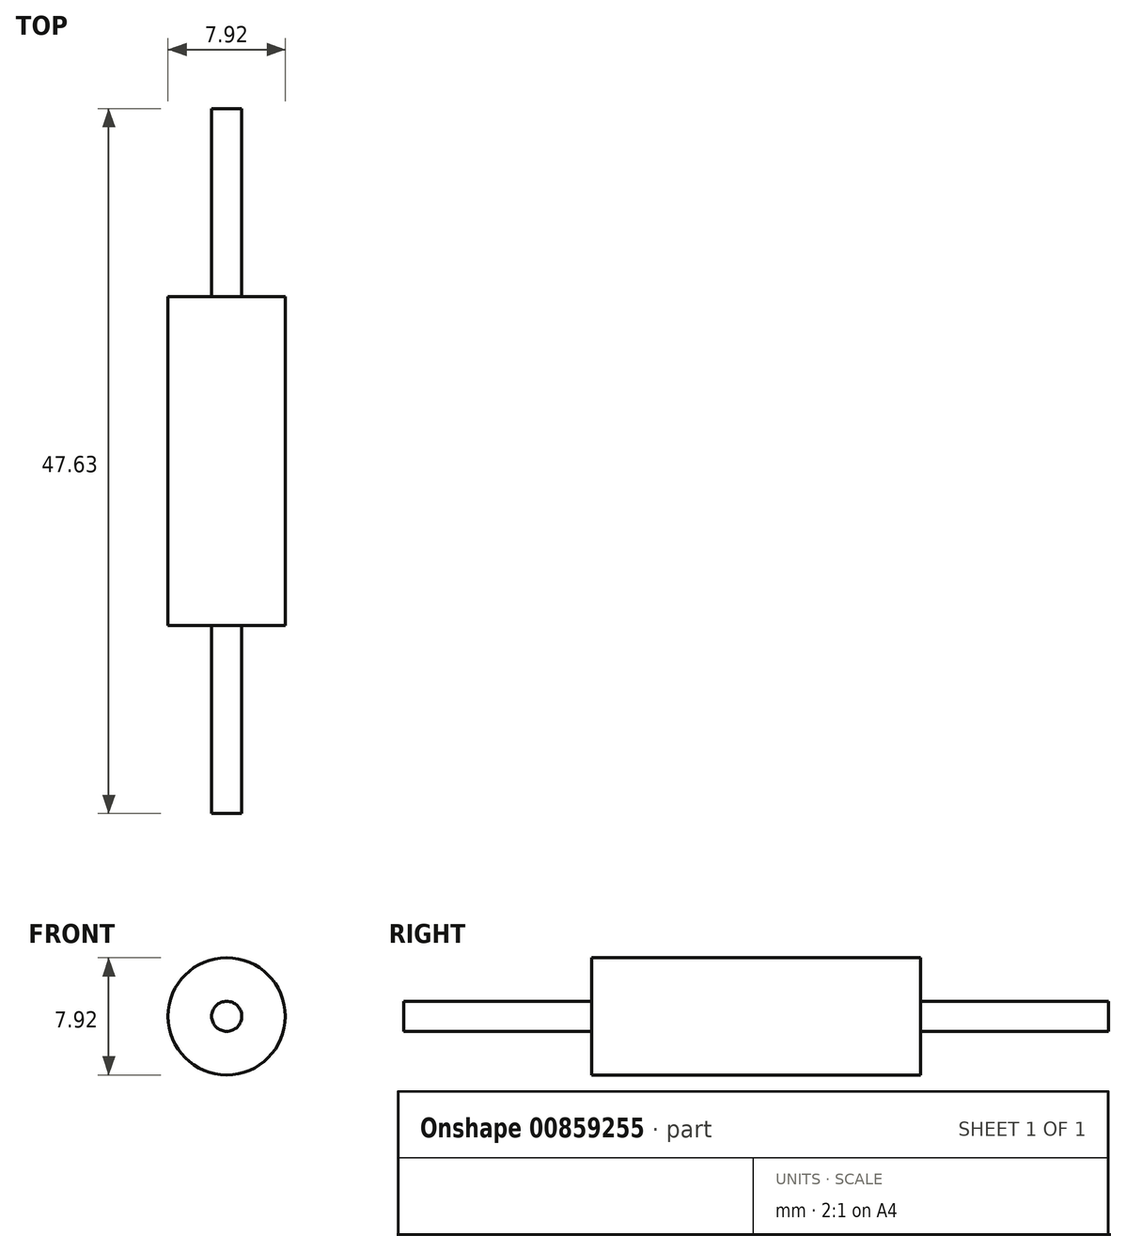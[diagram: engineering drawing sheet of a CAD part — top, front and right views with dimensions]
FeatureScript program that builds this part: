
annotation { "Feature Type Name" : "Feature", "Feature Type Description" : "" }
export const myFeature = defineFeature(function(context is Context, id is Id, definition is map)
    precondition{}
    {
        {
            var Q0;
            Q0=qCreatedBy(makeId("Front.planeOp"),FACE);
            var sketch = newSketch(context, id + "F0", { "sketchPlane" : qUnion([Q0])});
            skCircle(sketch, "E0", {"center": v(0, 0) * mm, "radius": 3.96 * mm});
            skSolve(sketch);
        }
        {
            var Q0;
            Q0 = qSketchRegion(id + "F0", true);
            extrude(context, id + "F1", {"entities" : qUnion([Q0]), "oppositeDirection" : true, "depth" : 22.22 * mm, "offsetDistance" : 25.4 * mm});
        }
        {
            var Q0;
            Q0=makeQuery(id+"F1.opExtrude","CAP_FACE",FACE,{"disambiguationData":[OSD([sQuery(id+"F0.wireOp",EDGE,"E0")])],"isStart":true});
            var sketch = newSketch(context, id + "F2", { "sketchPlane" : qUnion([Q0])});
            skCircle(sketch, "E1", {"center": v(0, 0) * mm, "radius": 1.02 * mm});
            skSolve(sketch);
        }
        {
            var Q0;
            Q0 = qSketchRegion(id + "F2", true);
            extrude(context, id + "F3", {"entities" : qUnion([Q0]), "operationType" : NewBodyOperationType.ADD, "depth" : 12.7 * mm, "offsetDistance" : 25.4 * mm});
        }
        {
            var Q0;
            Q0=makeQuery(id+"F1.opExtrude","CAP_FACE",FACE,{"disambiguationData":[OSD([sQuery(id+"F0.wireOp",EDGE,"E0")])],"isStart":false});
            var sketch = newSketch(context, id + "F4", { "sketchPlane" : qUnion([Q0])});
            skCircle(sketch, "E2", {"center": v(0, 0) * mm, "radius": 1.02 * mm});
            skSolve(sketch);
        }
        {
            var Q0;
            Q0 = qSketchRegion(id + "F4", true);
            extrude(context, id + "F5", {"entities" : qUnion([Q0]), "operationType" : NewBodyOperationType.ADD, "depth" : 12.7 * mm, "offsetDistance" : 25.4 * mm});
        }
    });
